# Revit family: IS_ConnectFreedom_E8240_BIM_DE
name_source: partatom
category: Plumbing Fixtures
revit_build: Autodesk Revit MEP 2015 (Build: 20140606_1530(x64)
units: mm (PartAtom-declared; Revit-internal decimal feet)

## types (1)
- E824001 - CONNECT FREEDOM XL seat & cover, slow close
    Assembly Code = C1030203
    BIMobject category = Toilet Seats
    BOSUseNativeGeometries = 1
    Brand url = http://www.idealstandard.co.uk
    Description = E824001 CONNECT FREEDOM XL seat & cover, slow close
    DrainSize = 0 mm  [stored 0 ft]
    EAN code = 5017830471196
    Edition number = 1
    FlushRate = 0 m³
    FlushingRate = 0
    IFC Classification = Sanitary Terminal
    IfcExportType = SEAT&COVER
    InletConnectionSize = 0 mm  [stored 0 ft]
    Installation instructions = http://www.idealstandard.de
    Manufacturer name = Ideal Standard
    ManufacturerURL = www.idealstandard.com
    Material = Duroplast
    Material main = Plastic
    MaterialThickness = 0 mm  [stored 0 ft]
    Model = E824001
    ModelNumber = E824001
    ModelReference = E824001
    Name = CONNECT FREEDOM XL seat & cover, slow close
    NettWeight = 2,1 kg
    Nominal height = 58
    Nominal width = 460
    NominalDepth = 488 mm  [stored 1.60105 ft]
    NominalHeight = 58 mm  [stored 0.190289 ft]
    NominalLength = 488 mm  [stored 1.60105 ft]
    NominalWidth = 460 mm  [stored 1.50919 ft]
    OmniClass Code = 23-31 19 19 17
    OmniClass Description = Water Closet Seats
    OutletConnectionSize = 0 mm  [stored 0 ft]
    Product Guid = 03d9c31d-8452-4e3d-83a6-1d1d498db567
    Product SKU = E8240
    Product data url = https://bimobject.com
    Product family = CONNECT FREEDOM
    Product group = WC Seats and covers
    Product name = CONNECT FREEDOM XL seat & cover, slow close
    Product url = http://www.idealstandard.de
    ProductInformation = www.idealstandard.de/produkte
    QR code = http://bimobject.com
    SeatColor = White
    SeatHasCover = No
    SeatMaterial = Duroplast
    Shape = Sculptured
    Size = 58x488x461
    Space = Internal
    SpareParts = www.idealstandard.de/ersatzteile
    Technical description = E824001 CONNECT FREEDOM XL seat & cover, slow close
    URL = www.idealstandard.com
    Uniclass 2015 Code = Pr_40_20_93_95
    Uniclass 2015 Name = WC seats and covers
    Uniclass2015Code = Pr_40_20_93_95
    Uniclass2015Title = WC seats and covers
    Version = 1
    VolumeUnits = Litres
    Weight Net (Kg) = 2.1

note: [stored X ft] marks values corroborated as IEEE doubles in the binary element streams (Revit-internal decimal feet)

## geometry (parser evidence)
native form markers: Blend x4, Sweep x1
no freeform markers — native parametric forms only
